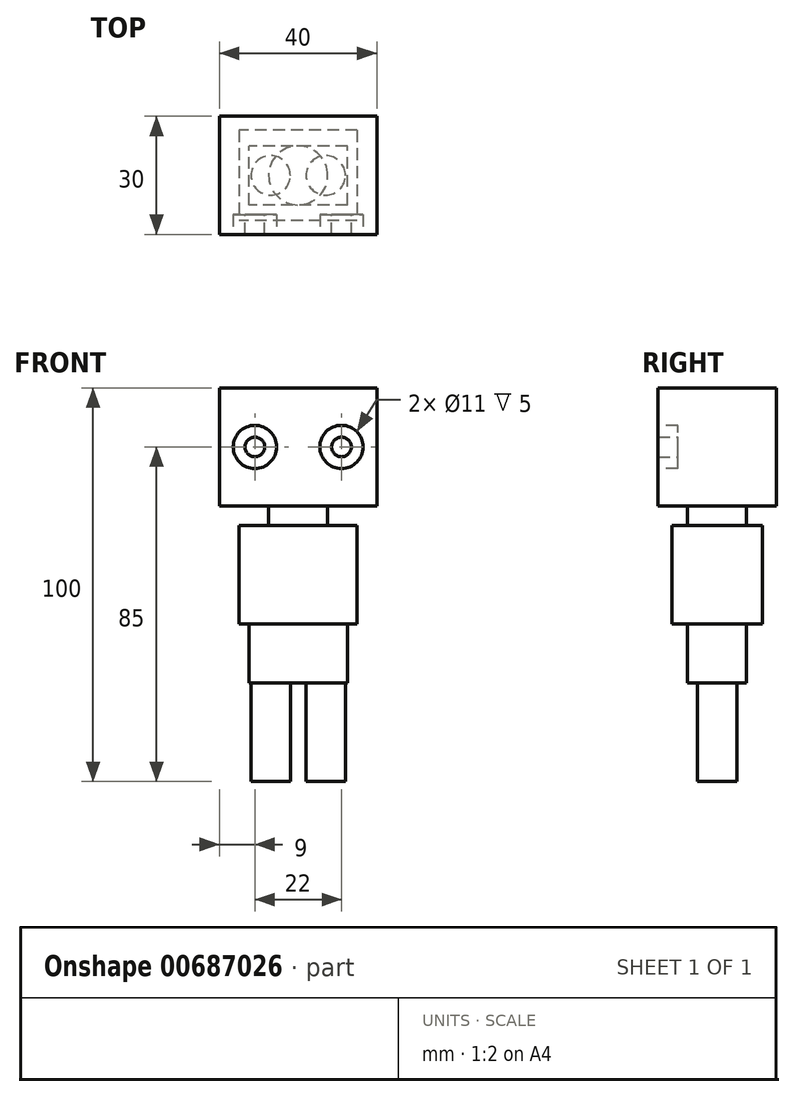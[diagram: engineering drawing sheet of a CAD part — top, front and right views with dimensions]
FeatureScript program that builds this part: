
annotation { "Feature Type Name" : "Feature", "Feature Type Description" : "" }
export const myFeature = defineFeature(function(context is Context, id is Id, definition is map)
    precondition{}
    {
        {
            var Q0;
            Q0=qCreatedBy(makeId("Top.planeOp"),FACE);
            var sketch = newSketch(context, id + "F0", { "sketchPlane" : qUnion([Q0])});
            skLineSegment(sketch, "E0.bottom", {"start": v(15, 11.5) * mm, "end": v(-15, 11.5) * mm});
            skLineSegment(sketch, "E0.top", {"start": v(15, -11.5) * mm, "end": v(-15, -11.5) * mm});
            skLineSegment(sketch, "E0.left", {"start": v(15, 11.5) * mm, "end": v(15, -11.5) * mm});
            skLineSegment(sketch, "E0.right", {"start": v(-15, 11.5) * mm, "end": v(-15, -11.5) * mm});
            skPoint(sketch, "E0.middle", {"position": v(0, 0) * mm});
            skSolve(sketch);
        }
        {
            var Q0;
            Q0 = qSketchRegion(id + "F0", true);
            extrude(context, id + "F1", {"entities" : qUnion([Q0]), "depth" : 25 * mm, "offsetDistance" : 25 * mm});
        }
        {
            var Q0;
            Q0=makeQuery(id+"F1.opExtrude","CAP_FACE",FACE,{"disambiguationData":[OSD([sQuery(id+"F0.wireOp",EDGE,"E0.bottom"),sQuery(id+"F0.wireOp",EDGE,"E0.top"),sQuery(id+"F0.wireOp",EDGE,"E0.left"),sQuery(id+"F0.wireOp",EDGE,"E0.right")])],"isStart":true});
            var sketch = newSketch(context, id + "F2", { "sketchPlane" : qUnion([Q0])});
            skLineSegment(sketch, "E1.bottom", {"start": v(12.5, 7.5) * mm, "end": v(-12.5, 7.5) * mm});
            skLineSegment(sketch, "E1.top", {"start": v(12.5, -7.5) * mm, "end": v(-12.5, -7.5) * mm});
            skLineSegment(sketch, "E1.left", {"start": v(12.5, 7.5) * mm, "end": v(12.5, -7.5) * mm});
            skLineSegment(sketch, "E1.right", {"start": v(-12.5, 7.5) * mm, "end": v(-12.5, -7.5) * mm});
            skPoint(sketch, "E1.middle", {"position": v(0, 0) * mm});
            skSolve(sketch);
        }
        {
            var Q0;
            Q0 = qSketchRegion(id + "F2", true);
            extrude(context, id + "F3", {"entities" : qUnion([Q0]), "operationType" : NewBodyOperationType.ADD, "depth" : 15 * mm, "offsetDistance" : 25 * mm});
        }
        {
            var Q0;
            Q0=makeQuery(id+"F3.opExtrude","CAP_FACE",FACE,{"disambiguationData":[OSD([sQuery(id+"F2.wireOp",EDGE,"E1.bottom"),sQuery(id+"F2.wireOp",EDGE,"E1.top"),sQuery(id+"F2.wireOp",EDGE,"E1.left"),sQuery(id+"F2.wireOp",EDGE,"E1.right")])],"isStart":false});
            var sketch = newSketch(context, id + "F4", { "sketchPlane" : qUnion([Q0])});
            skCircle(sketch, "E2", {"center": v(7, 0) * mm, "radius": 5 * mm});
            skCircle(sketch, "E3", {"center": v(-7, 0) * mm, "radius": 5 * mm});
            skSolve(sketch);
        }
        {
            var Q0;
            Q0 = qSketchRegion(id + "F4", true);
            extrude(context, id + "F5", {"entities" : qUnion([Q0]), "operationType" : NewBodyOperationType.ADD, "depth" : 25 * mm, "offsetDistance" : 25 * mm});
        }
        {
            var Q0;
            Q0=makeQuery(id+"F1.opExtrude","CAP_FACE",FACE,{"disambiguationData":[OSD([sQuery(id+"F0.wireOp",EDGE,"E0.bottom"),sQuery(id+"F0.wireOp",EDGE,"E0.top"),sQuery(id+"F0.wireOp",EDGE,"E0.left"),sQuery(id+"F0.wireOp",EDGE,"E0.right")])],"isStart":false});
            var sketch = newSketch(context, id + "F6", { "sketchPlane" : qUnion([Q0])});
            skCircle(sketch, "E4", {"center": v(0, 0) * mm, "radius": 7.5 * mm});
            skSolve(sketch);
        }
        {
            var Q0;
            Q0 = qSketchRegion(id + "F6", true);
            extrude(context, id + "F7", {"entities" : qUnion([Q0]), "operationType" : NewBodyOperationType.ADD, "depth" : 5 * mm, "offsetDistance" : 25 * mm});
        }
        {
            var Q0;
            Q0=makeQuery(id+"F7.opExtrude","CAP_FACE",FACE,{"disambiguationData":[OSD([sQuery(id+"F6.wireOp",EDGE,"E4")])],"isStart":false});
            var sketch = newSketch(context, id + "F8", { "sketchPlane" : qUnion([Q0])});
            skLineSegment(sketch, "E5.bottom", {"start": v(20, 15) * mm, "end": v(-20, 15) * mm});
            skLineSegment(sketch, "E5.top", {"start": v(20, -15) * mm, "end": v(-20, -15) * mm});
            skLineSegment(sketch, "E5.left", {"start": v(20, 15) * mm, "end": v(20, -15) * mm});
            skLineSegment(sketch, "E5.right", {"start": v(-20, 15) * mm, "end": v(-20, -15) * mm});
            skPoint(sketch, "E5.middle", {"position": v(0, 0) * mm});
            skSolve(sketch);
        }
        {
            var Q0;
            Q0 = qSketchRegion(id + "F8", true);
            extrude(context, id + "F9", {"entities" : qUnion([Q0]), "operationType" : NewBodyOperationType.ADD, "depth" : 30 * mm, "offsetDistance" : 25 * mm});
        }
        {
            var Q0;
            Q0=makeQuery(id+"F9.opExtrude","SWEPT_FACE",FACE,{"disambiguationData":[OSD([sQuery(id+"F8.wireOp",EDGE,"E5.top")])]});
            var sketch = newSketch(context, id + "F10", { "sketchPlane" : qUnion([Q0])});
            skCircle(sketch, "E6", {"center": v(-11, 45) * mm, "radius": 5.5 * mm});
            skCircle(sketch, "E7", {"center": v(11, 45) * mm, "radius": 5.5 * mm});
            skSolve(sketch);
        }
        {
            var Q0;
            Q0 = qSketchRegion(id + "F10", true);
            extrude(context, id + "F11", {"entities" : qUnion([Q0]), "operationType" : NewBodyOperationType.REMOVE, "oppositeDirection" : true, "depth" : 5 * mm, "offsetDistance" : 25 * mm});
        }
        {
            var Q0;
            Q0=makeQuery(id+"F11.boolean.opBoolean","COPY",FACE,{"derivedFrom":makeQuery(id+"F11.opExtrude","CAP_FACE",FACE,{"disambiguationData":[OSD([sQuery(id+"F10.wireOp",EDGE,"E6")])],"isStart":false})});
            var sketch = newSketch(context, id + "F12", { "sketchPlane" : qUnion([Q0])});
            skCircle(sketch, "E8", {"center": v(-11, 45) * mm, "radius": 2.5 * mm});
            skSolve(sketch);
        }
        {
            var Q0;
            Q0 = qSketchRegion(id + "F12", true);
            extrude(context, id + "F13", {"entities" : qUnion([Q0]), "operationType" : NewBodyOperationType.ADD, "depth" : 5 * mm, "offsetDistance" : 25 * mm});
        }
        {
            var Q0;
            Q0=makeQuery(id+"F11.boolean.opBoolean","COPY",FACE,{"derivedFrom":makeQuery(id+"F11.opExtrude","CAP_FACE",FACE,{"disambiguationData":[OSD([sQuery(id+"F10.wireOp",EDGE,"E7")])],"isStart":false})});
            var sketch = newSketch(context, id + "F14", { "sketchPlane" : qUnion([Q0])});
            skCircle(sketch, "E9", {"center": v(11, 45) * mm, "radius": 2.5 * mm});
            skSolve(sketch);
        }
        {
            var Q0;
            Q0 = qSketchRegion(id + "F14", true);
            extrude(context, id + "F15", {"entities" : qUnion([Q0]), "operationType" : NewBodyOperationType.ADD, "depth" : 5 * mm, "offsetDistance" : 25 * mm});
        }
    });
